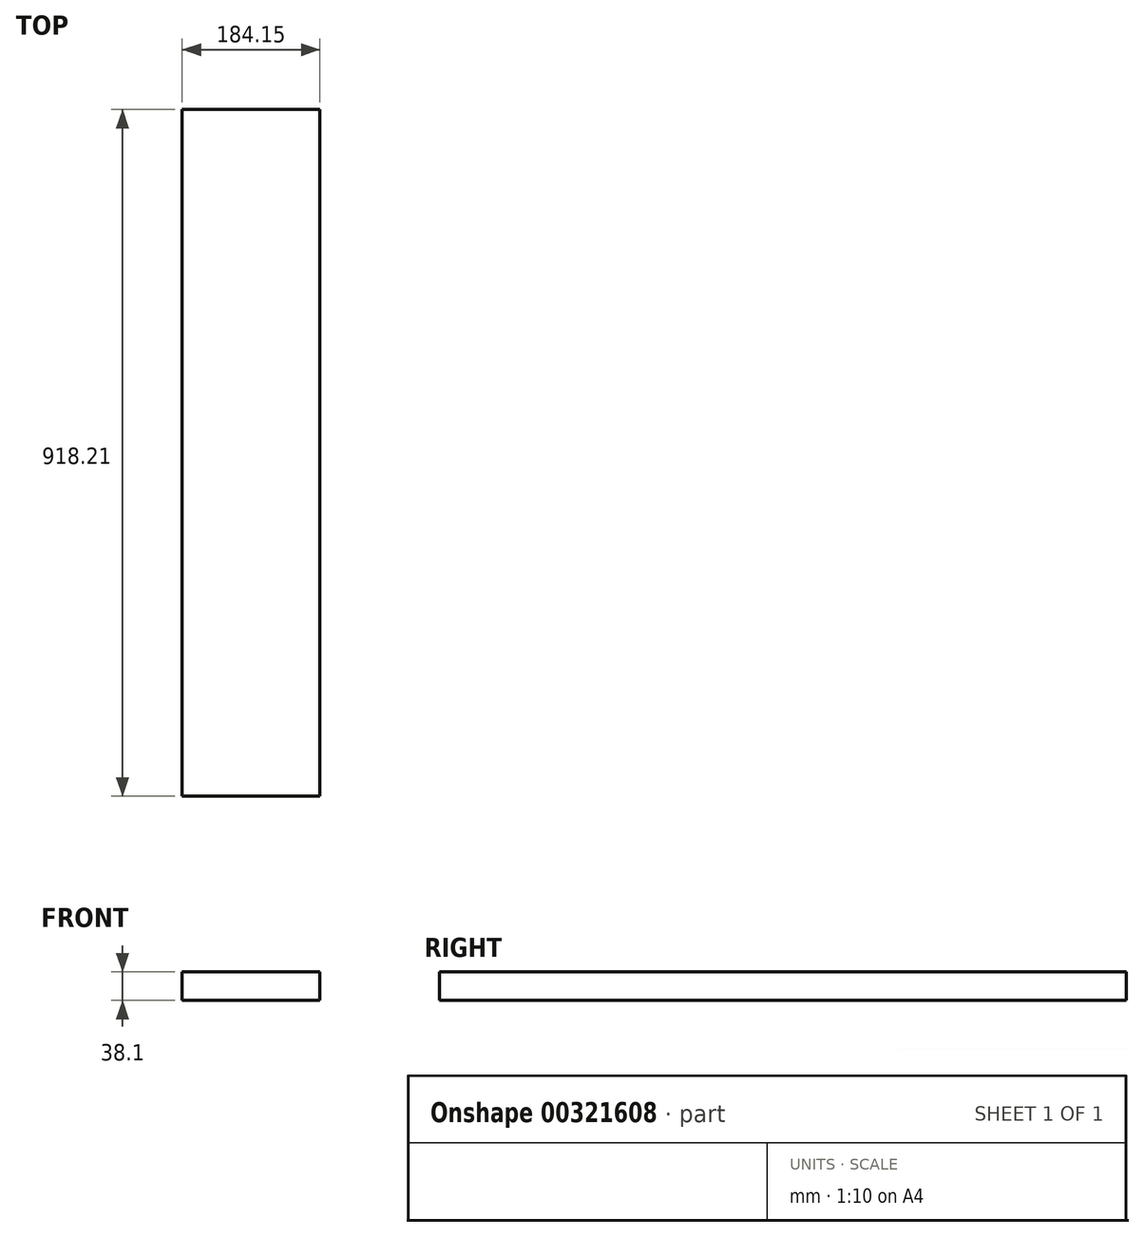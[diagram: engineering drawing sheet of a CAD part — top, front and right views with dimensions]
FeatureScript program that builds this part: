
annotation { "Feature Type Name" : "Feature", "Feature Type Description" : "" }
export const myFeature = defineFeature(function(context is Context, id is Id, definition is map)
    precondition{}
    {
        {
            var Q0;
            Q0=qCreatedBy(makeId("Front.planeOp"),FACE);
            var sketch = newSketch(context, id + "F0", { "sketchPlane" : qUnion([Q0])});
            skLineSegment(sketch, "E0.bottom", {"start": v(-184.15, 0) * mm, "end": v(0, 0) * mm});
            skLineSegment(sketch, "E0.top", {"start": v(-184.15, -38.1) * mm, "end": v(0, -38.1) * mm});
            skLineSegment(sketch, "E0.left", {"start": v(-184.15, 0) * mm, "end": v(-184.15, -38.1) * mm});
            skLineSegment(sketch, "E0.right", {"start": v(0, 0) * mm, "end": v(0, -38.1) * mm});
            skSolve(sketch);
        }
        {
            var Q0;
            Q0=makeQuery(id+"F0.imprint","IMPRINT",FACE,{"disambiguationData":[TD([[makeQuery(id+"F0.imprint","IMPRINT",EDGE,{"derivedFrom":sQuery(id+"F0.wireOp",EDGE,"E0.bottom")}),-1.0]])]});
            extrude(context, id + "F1", {"entities" : qUnion([Q0]), "depth" : 918.2 * mm});
        }
    });
